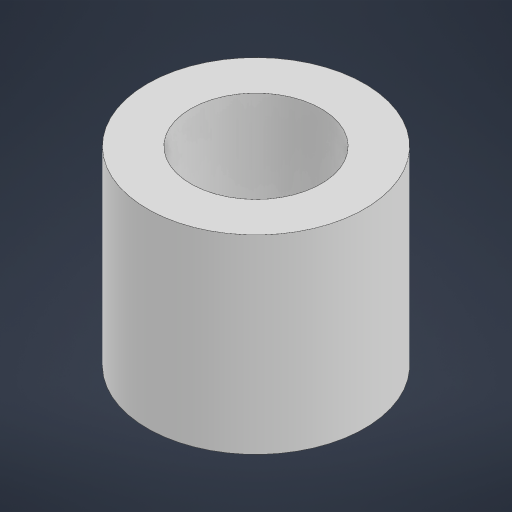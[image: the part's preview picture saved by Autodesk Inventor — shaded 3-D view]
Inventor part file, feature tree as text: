
AUTODESK INVENTOR PART (.ipt)
format: ipt  version: 2024.2 (Build 282272000, 272)  size: 151,552 bytes
history: native  units: mm
features: extrude x1, sketch x1
ambient origin geometry x8: Origin, YZ Plane, XZ Plane, XY Plane, X Axis, Y Axis, Z Axis, Center Point
bodies: Solid1 (feature_tree)
feature tree (2):
  extrude  "Extrusion1"  Depth=3.5mm
  sketch  "Sketch1"  dims[d0=2.4mm d1=4.0mm d2=3.5mm d3=0.0mm]
